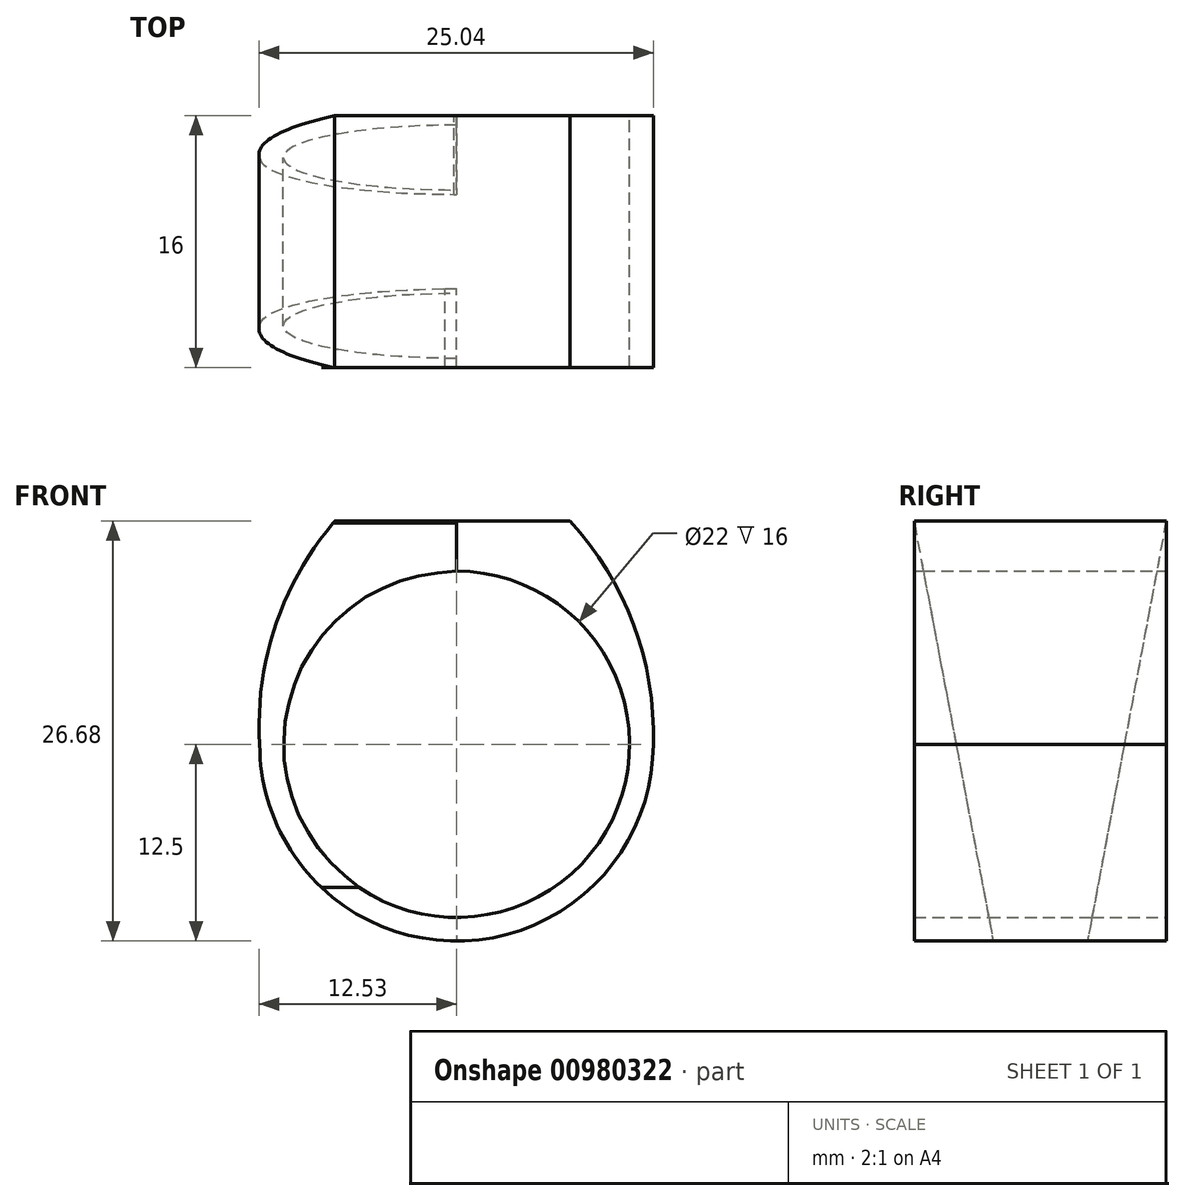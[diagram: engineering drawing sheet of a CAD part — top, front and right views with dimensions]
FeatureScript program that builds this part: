
annotation { "Feature Type Name" : "Feature", "Feature Type Description" : "" }
export const myFeature = defineFeature(function(context is Context, id is Id, definition is map)
    precondition{}
    {
        {
            var Q0;
            Q0=qCreatedBy(makeId("Front.planeOp"),FACE);
            var sketch = newSketch(context, id + "F0", { "sketchPlane" : qUnion([Q0])});
            skCircle(sketch, "E0", {"center": v(0, 0) * mm, "radius": 12.5 * mm});
            skCircle(sketch, "E1", {"center": v(0, 0) * mm, "radius": 11 * mm});
            skSolve(sketch);
        }
        {
            var Q0;
            Q0 = qSketchRegion(id + "FotlYpZr0T40TRP_1", true);
            var Q1;
            Q1 = qSketchRegion(id + "F0", true);
            extrude(context, id + "F1", {"entities" : qUnion([Q0, Q1]), "depth" : 16 * mm, "offsetDistance" : 25 * mm});
        }
        {
            var Q0;
            Q0=qCreatedBy(makeId("Front.planeOp"),FACE);
            var sketch = newSketch(context, id + "F2", { "sketchPlane" : qUnion([Q0])});
            skLineSegment(sketch, "E2.bottom", {"start": v(-7.73, 14.18) * mm, "end": v(7.2, 14.18) * mm});
            skLineSegment(sketch, "E3", {"start": v(-7.73, 14.18) * mm, "end": v(-7.73, 9.76) * mm});
            skLineSegment(sketch, "E4", {"start": v(7.2, 14.18) * mm, "end": v(7.2, 10.18) * mm});
            skArc(sketch, "E5", {"start": v(-7.73, 9.76) * mm, "mid": v(4.14, -11.5) * mm, "end": v(0, 12.5) * mm});
            skSolve(sketch);
        }
        {
            var Q0;
            Q0 = qSketchRegion(id + "F2", true);
            extrude(context, id + "F3", {"entities" : qUnion([Q0]), "operationType" : NewBodyOperationType.ADD, "depth" : 16 * mm, "offsetDistance" : 25 * mm});
        }
        {
            var Q0;
            Q0=makeQuery(id+"F0.imprint","IMPRINT",FACE,{"disambiguationData":[TD([[makeQuery(id+"F0.imprint","IMPRINT",EDGE,{"derivedFrom":sQuery(id+"F0.wireOp",EDGE,"E1")}),1.0]])]});
            extrude(context, id + "F4", {"entities" : qUnion([Q0]), "operationType" : NewBodyOperationType.REMOVE, "depth" : 26 * mm, "offsetDistance" : 25 * mm});
        }
        {
            var Q0;
            Q0=makeQuery(id+"F3.boolean.opBoolean","MERGE",FACE,{"derivedFrom":[makeQuery(id+"F1.opExtrude","CAP_FACE",FACE,{"disambiguationData":[OSD([sQuery(id+"F0.wireOp",EDGE,"E0"),sQuery(id+"F0.wireOp",EDGE,"E1")])],"isStart":false}),makeQuery(id+"F3.opExtrude","CAP_FACE",FACE,{"disambiguationData":[OSD([sQuery(id+"F2.wireOp",EDGE,"E2.bottom"),sQuery(id+"F2.wireOp",EDGE,"E3"),sQuery(id+"F2.wireOp",EDGE,"E4"),sQuery(id+"F2.wireOp",EDGE,"E5")])],"isStart":false})]});
            var sketch = newSketch(context, id + "F5", { "sketchPlane" : qUnion([Q0])});
            skArc(sketch, "E6", {"start": v(12.5, 0) * mm, "mid": v(11.25, 7.61) * mm, "end": v(7.2, 14.18) * mm});
            skArc(sketch, "E7", {"start": v(-7.73, 14.18) * mm, "mid": v(-11.5, 7.55) * mm, "end": v(-12.5, 0) * mm});
            skSolve(sketch);
        }
        {
            var Q0;
            {var subQ0=sQuery(id+"F5.wireOp",EDGE,"E7");Q0=makeQuery(id+"F5.imprint","IMPRINT",FACE,{"disambiguationData":[TD([[makeQuery(id+"F5.imprint","IMPRINT",EDGE,{"derivedFrom":subQ0}),1.0]])]});}
            var Q1;
            {var subQ0=sQuery(id+"F5.wireOp",EDGE,"E6");Q1=makeQuery(id+"F5.imprint","IMPRINT",FACE,{"disambiguationData":[TD([[makeQuery(id+"F5.imprint","IMPRINT",EDGE,{"derivedFrom":subQ0}),1.0]])]});}
            extrude(context, id + "F6", {"entities" : qUnion([Q0, Q1]), "operationType" : NewBodyOperationType.ADD, "oppositeDirection" : true, "depth" : 16 * mm, "offsetDistance" : 25 * mm});
        }
        {
            var Q0;
            Q0=qCreatedBy(makeId("Right.planeOp"),FACE);
            var sketch = newSketch(context, id + "F7", { "sketchPlane" : qUnion([Q0])});
            skLineSegment(sketch, "E8", {"start": v(-16, -12.48) * mm, "end": v(-11, -12.48) * mm});
            skLineSegment(sketch, "E9", {"start": v(0, -12.5) * mm, "end": v(-5, -12.5) * mm});
            skLineSegment(sketch, "E10", {"start": v(-16.03, 14.22) * mm, "end": v(-11, -12.48) * mm});
            skLineSegment(sketch, "E11", {"start": v(0, 14.22) * mm, "end": v(-5, -12.5) * mm});
            skLineSegment(sketch, "E12", {"start": v(-16.03, 14.22) * mm, "end": v(-16, -12.48) * mm});
            skLineSegment(sketch, "E13", {"start": v(0, 14.22) * mm, "end": v(0, -12.5) * mm});
            skSolve(sketch);
        }
        {
            var Q0;
            Q0=makeQuery(id+"F7.imprint","IMPRINT",FACE,{"disambiguationData":[TD([[makeQuery(id+"F7.imprint","IMPRINT",EDGE,{"derivedFrom":sQuery(id+"F7.wireOp",EDGE,"E8")}),1.0]])]});
            var Q1;
            Q1=makeQuery(id+"F7.imprint","IMPRINT",FACE,{"disambiguationData":[TD([[makeQuery(id+"F7.imprint","IMPRINT",EDGE,{"derivedFrom":sQuery(id+"F7.wireOp",EDGE,"E9")}),-1.0]])]});
            extrude(context, id + "F8", {"entities" : qUnion([Q0, Q1]), "operationType" : NewBodyOperationType.REMOVE, "oppositeDirection" : true, "depth" : 15 * mm, "offsetDistance" : 25 * mm});
        }
    });
